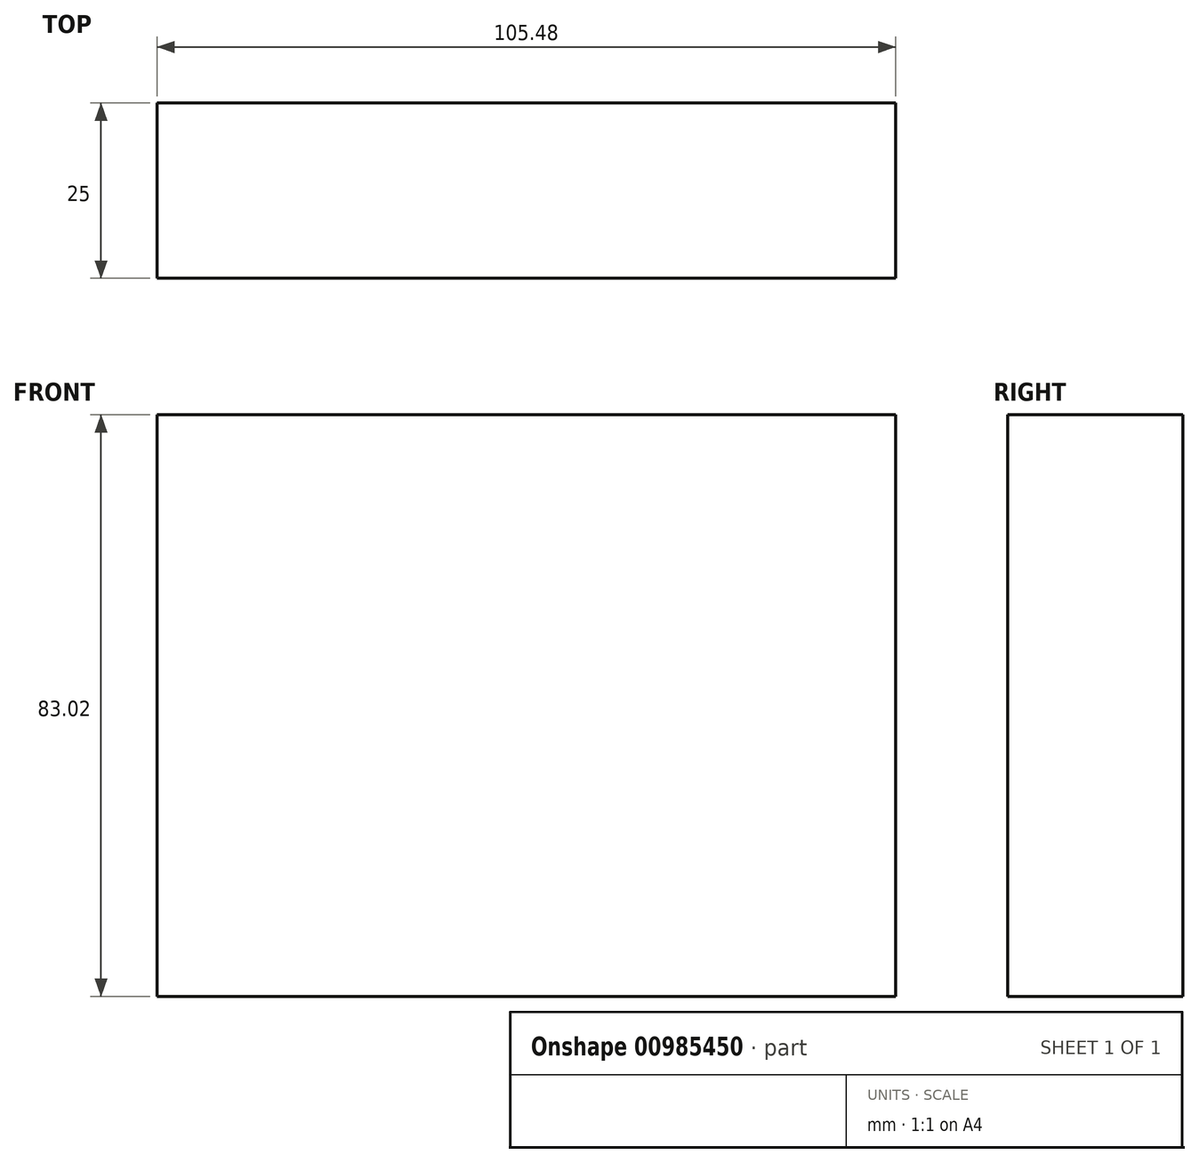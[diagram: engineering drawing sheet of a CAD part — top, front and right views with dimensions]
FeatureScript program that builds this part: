
annotation { "Feature Type Name" : "Feature", "Feature Type Description" : "" }
export const myFeature = defineFeature(function(context is Context, id is Id, definition is map)
    precondition{}
    {
        {
            var Q0;
            Q0=qCreatedBy(makeId("Front.planeOp"),FACE);
            var sketch = newSketch(context, id + "F0", { "sketchPlane" : qUnion([Q0])});
            skLineSegment(sketch, "E0.bottom", {"start": v(-52.74, 41.51) * mm, "end": v(52.74, 41.51) * mm});
            skLineSegment(sketch, "E0.top", {"start": v(-52.74, -41.51) * mm, "end": v(52.74, -41.51) * mm});
            skLineSegment(sketch, "E0.left", {"start": v(-52.74, 41.51) * mm, "end": v(-52.74, -41.51) * mm});
            skLineSegment(sketch, "E0.right", {"start": v(52.74, 41.51) * mm, "end": v(52.74, -41.51) * mm});
            skPoint(sketch, "E0.middle", {"position": v(0, 0) * mm});
            skSolve(sketch);
        }
        {
            var Q0;
            Q0=makeQuery(id+"F0.imprint","IMPRINT",FACE,{"disambiguationData":[TD([[makeQuery(id+"F0.imprint","IMPRINT",EDGE,{"derivedFrom":sQuery(id+"F0.wireOp",EDGE,"E0.bottom")}),-1.0]])]});
            extrude(context, id + "F1", {"entities" : qUnion([Q0]), "depth" : 25 * mm, "offsetDistance" : 25 * mm});
        }
    });
